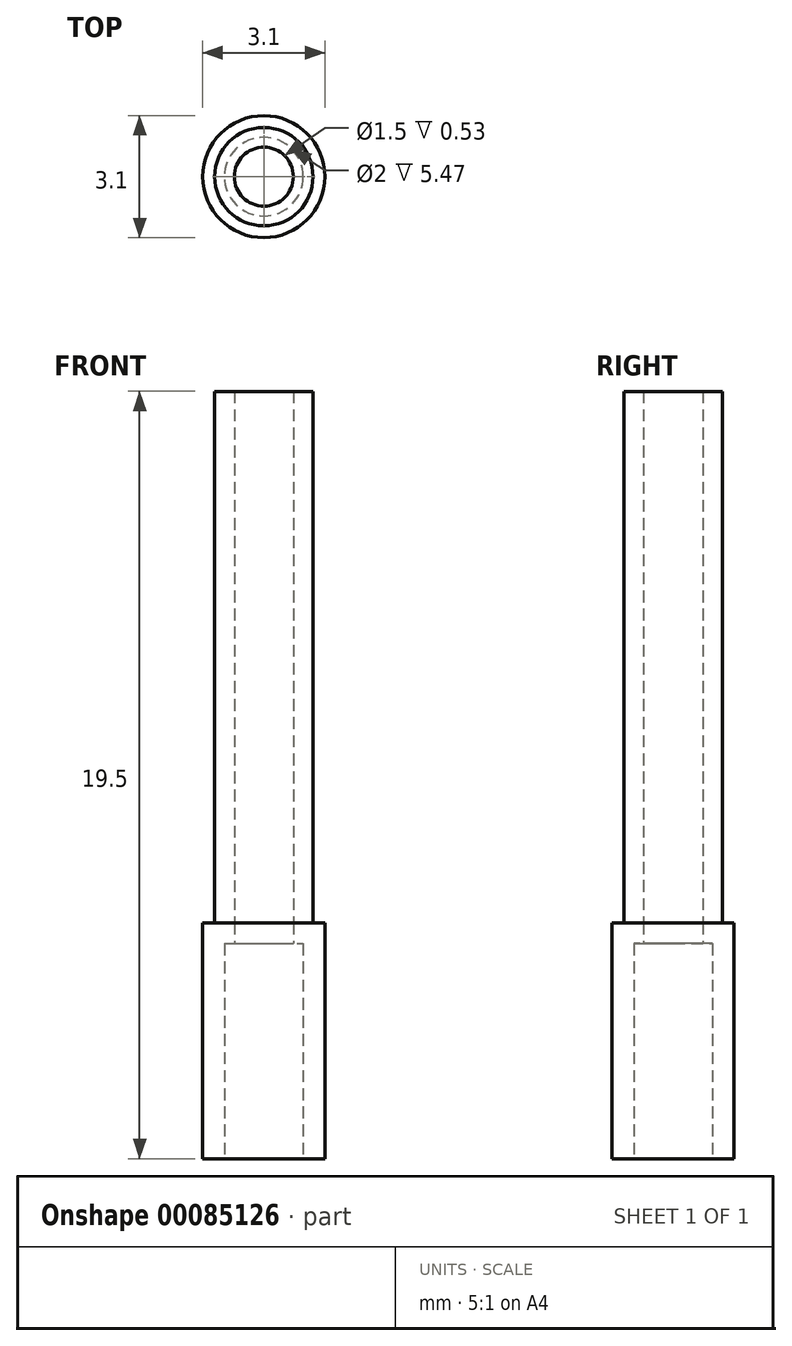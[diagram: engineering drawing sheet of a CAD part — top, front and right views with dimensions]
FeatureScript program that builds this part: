
annotation { "Feature Type Name" : "Feature", "Feature Type Description" : "" }
export const myFeature = defineFeature(function(context is Context, id is Id, definition is map)
    precondition{}
    {
        {
            var Q0;
            Q0=qCreatedBy(makeId("Front.planeOp"),FACE);
            var sketch = newSketch(context, id + "F0", { "sketchPlane" : qUnion([Q0])});
            skLineSegment(sketch, "E0.bottom", {"start": v(1.55, -6.6) * mm, "end": v(-1.55, -6.6) * mm});
            skLineSegment(sketch, "E0.top", {"start": v(1.55, -0.6) * mm, "end": v(-1.55, -0.6) * mm});
            skLineSegment(sketch, "E0.left", {"start": v(1.55, -6.6) * mm, "end": v(1.55, -0.6) * mm});
            skLineSegment(sketch, "E0.right", {"start": v(-1.55, -6.6) * mm, "end": v(-1.55, -0.6) * mm});
            skLineSegment(sketch, "E1.bottom", {"start": v(1, -6.6) * mm, "end": v(-1, -6.6) * mm});
            skLineSegment(sketch, "E1.top", {"start": v(1, -1.13) * mm, "end": v(-1, -1.13) * mm});
            skLineSegment(sketch, "E1.left", {"start": v(1, -6.6) * mm, "end": v(1, -1.13) * mm});
            skLineSegment(sketch, "E1.right", {"start": v(-1, -6.6) * mm, "end": v(-1, -1.13) * mm});
            skLineSegment(sketch, "E2.bottom", {"start": v(1.25, -0.6) * mm, "end": v(-1.25, -0.6) * mm});
            skLineSegment(sketch, "E2.top", {"start": v(1.25, 12.9) * mm, "end": v(-1.25, 12.9) * mm});
            skLineSegment(sketch, "E2.left", {"start": v(1.25, -0.6) * mm, "end": v(1.25, 12.9) * mm});
            skLineSegment(sketch, "E2.right", {"start": v(-1.25, -0.6) * mm, "end": v(-1.25, 12.9) * mm});
            skLineSegment(sketch, "E3", {"start": v(0, -0.6) * mm, "end": v(0, 12.9) * mm});
            skLineSegment(sketch, "E4", {"start": v(0, -6.6) * mm, "end": v(0, -0.6) * mm});
            skLineSegment(sketch, "E5", {"start": v(0, -0.6) * mm, "end": v(0, 6.15) * mm});
            skLineSegment(sketch, "E6.bottom", {"start": v(0.75, -0.6) * mm, "end": v(-0.75, -0.6) * mm});
            skLineSegment(sketch, "E6.top", {"start": v(0.75, 12.9) * mm, "end": v(-0.75, 12.9) * mm});
            skLineSegment(sketch, "E6.left", {"start": v(0.75, -0.6) * mm, "end": v(0.75, 12.9) * mm});
            skLineSegment(sketch, "E6.right", {"start": v(-0.75, -0.6) * mm, "end": v(-0.75, 12.9) * mm});
            skLineSegment(sketch, "E7", {"start": v(-0.75, -0.6) * mm, "end": v(-0.75, -1.13) * mm});
            skLineSegment(sketch, "E8", {"start": v(0.75, -0.6) * mm, "end": v(0.75, -1.13) * mm});
            skSolve(sketch);
        }
        {
            var Q0;
            {var subQ3=sQuery(id+"F0.wireOp",EDGE,"E0.right");Q0=makeQuery(id+"F0.imprint","IMPRINT",FACE,{"disambiguationData":[TD([[makeQuery(id+"F0.imprint","IMPRINT",EDGE,{"derivedFrom":subQ3}),-1.0]])]});}
            var Q1;
            Q1=sQuery(id+"F0.wireOp",EDGE,"E4");
            var Q2;
            Q2=sQuery(id+"F0.wireOp",EDGE,"E4");
            revolve(context, id + "F1", {"entities" : qUnion([Q0]), "surfaceEntities" : qUnion([Q1]), "axis" : qUnion([Q2]), "revolveType" : RevolveType.FULL});
        }
        {
            var Q0;
            {var subQ0=sQuery(id+"F0.wireOp",EDGE,"E2.right");Q0=makeQuery(id+"F0.imprint","IMPRINT",FACE,{"disambiguationData":[TD([[makeQuery(id+"F0.imprint","IMPRINT",EDGE,{"derivedFrom":subQ0}),-1.0]])]});}
            var Q1;
            Q1=sQuery(id+"F0.wireOp",EDGE,"E3");
            revolve(context, id + "F2", {"entities" : qUnion([Q0]), "axis" : qUnion([Q1]), "revolveType" : RevolveType.FULL});
        }
    });
